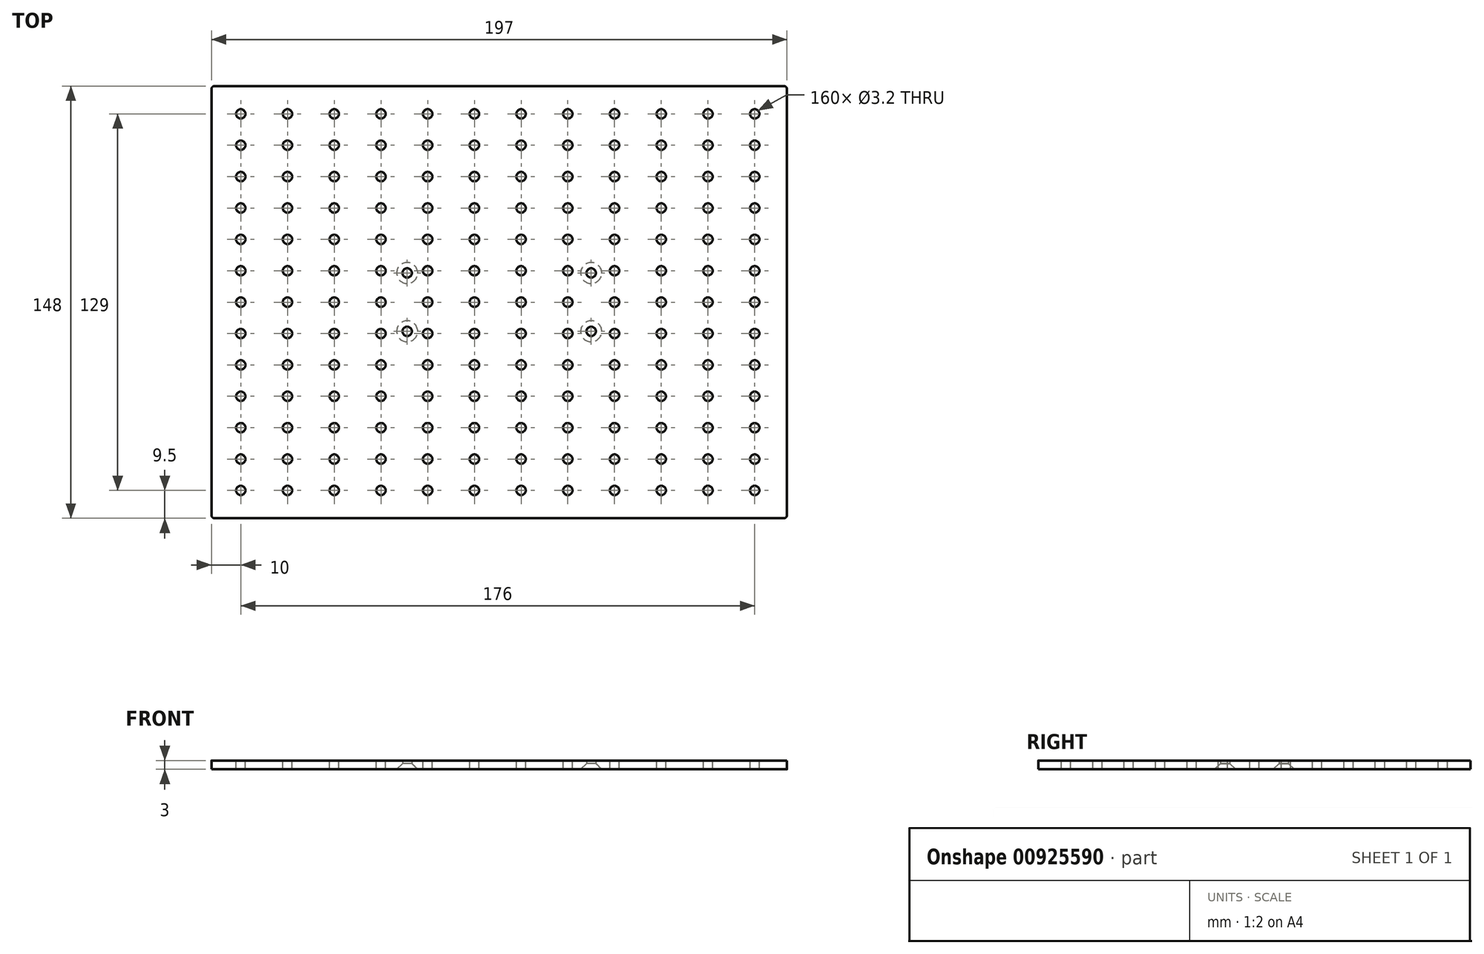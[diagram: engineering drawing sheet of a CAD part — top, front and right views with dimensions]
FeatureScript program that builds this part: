
annotation { "Feature Type Name" : "Feature", "Feature Type Description" : "" }
export const myFeature = defineFeature(function(context is Context, id is Id, definition is map)
    precondition{}
    {
        {
            var Q0;
            Q0=qCreatedBy(makeId("Top.planeOp"),FACE);
            var sketch = newSketch(context, id + "F0", { "sketchPlane" : qUnion([Q0])});
            skLineSegment(sketch, "E0.bottom", {"start": v(98.5, -74) * mm, "end": v(-98.5, -74) * mm});
            skLineSegment(sketch, "E0.top", {"start": v(98.5, 74) * mm, "end": v(-98.5, 74) * mm});
            skLineSegment(sketch, "E0.left", {"start": v(98.5, -74) * mm, "end": v(98.5, 74) * mm});
            skLineSegment(sketch, "E0.right", {"start": v(-98.5, -74) * mm, "end": v(-98.5, 74) * mm});
            skPoint(sketch, "E0.middle", {"position": v(0, 0) * mm});
            skLineSegment(sketch, "E1", {"start": v(0, 19.57) * mm, "end": v(0, -20.96) * mm, "construction": true});
            skLineSegment(sketch, "E2", {"start": v(-19.34, 0) * mm, "end": v(20.32, 0) * mm, "construction": true});
            skCircle(sketch, "E3", {"center": v(-31.5, 10) * mm, "radius": 1.6 * mm});
            skCircle(sketch, "E4", {"center": v(31.5, 10) * mm, "radius": 1.6 * mm});
            skCircle(sketch, "E5", {"center": v(31.5, -10) * mm, "radius": 1.6 * mm});
            skCircle(sketch, "E6", {"center": v(-31.5, -10) * mm, "radius": 1.6 * mm});
            skSolve(sketch);
        }
        {
            var Q0;
            Q0 = qSketchRegion(id + "F0", true);
            extrude(context, id + "F1", {"entities" : qUnion([Q0]), "depth" : 3 * mm, "offsetDistance" : 25 * mm});
        }
        {
            var Q0;
            Q0=makeQuery(id+"F1.opExtrude","CAP_FACE",FACE,{"disambiguationData":[OSD([sQuery(id+"F0.wireOp",EDGE,"E0.bottom"),sQuery(id+"F0.wireOp",EDGE,"E0.top"),sQuery(id+"F0.wireOp",EDGE,"E0.left"),sQuery(id+"F0.wireOp",EDGE,"E0.right"),sQuery(id+"F0.wireOp",EDGE,"E3"),sQuery(id+"F0.wireOp",EDGE,"E4"),sQuery(id+"F0.wireOp",EDGE,"E5"),sQuery(id+"F0.wireOp",EDGE,"E6")])],"isStart":false});
            var sketch = newSketch(context, id + "F2", { "sketchPlane" : qUnion([Q0])});
            skCircle(sketch, "E7", {"center": v(-88.5, 0) * mm, "radius": 1.6 * mm});
            skLineSegment(sketch, "E8.direction1", {"start": v(-88.5, 0) * mm, "end": v(-70.75, 0) * mm, "construction": true});
            skCircle(sketch, "E9.0.1.0", {"center": v(-88.5, 10.75) * mm, "radius": 1.6 * mm});
            skCircle(sketch, "E9.0.2.0", {"center": v(-88.5, 21.5) * mm, "radius": 1.6 * mm});
            skCircle(sketch, "E9.0.3.0", {"center": v(-88.5, 32.25) * mm, "radius": 1.6 * mm});
            skCircle(sketch, "E9.0.4.0", {"center": v(-88.5, 43) * mm, "radius": 1.6 * mm});
            skCircle(sketch, "E9.0.5.0", {"center": v(-88.5, 53.75) * mm, "radius": 1.6 * mm});
            skCircle(sketch, "E9.0.6.0", {"center": v(-88.5, 64.5) * mm, "radius": 1.6 * mm});
            skLineSegment(sketch, "E9.direction1", {"start": v(-88.5, 0) * mm, "end": v(-63.5, 0) * mm, "construction": true});
            skLineSegment(sketch, "E9.direction2", {"start": v(-88.5, 0) * mm, "end": v(-88.5, 10.75) * mm, "construction": true});
            skCircle(sketch, "E10.0.1.0", {"center": v(-88.5, -10.75) * mm, "radius": 1.6 * mm});
            skCircle(sketch, "E10.0.2.0", {"center": v(-88.5, -21.5) * mm, "radius": 1.6 * mm});
            skCircle(sketch, "E10.0.3.0", {"center": v(-88.5, -32.25) * mm, "radius": 1.6 * mm});
            skCircle(sketch, "E10.0.4.0", {"center": v(-88.5, -43) * mm, "radius": 1.6 * mm});
            skCircle(sketch, "E10.0.5.0", {"center": v(-88.5, -53.75) * mm, "radius": 1.6 * mm});
            skCircle(sketch, "E10.0.6.0", {"center": v(-88.5, -64.5) * mm, "radius": 1.6 * mm});
            skLineSegment(sketch, "E10.direction2", {"start": v(-88.5, 0) * mm, "end": v(-88.5, -10.75) * mm, "construction": true});
            skCircle(sketch, "E11.1.0.0", {"center": v(-72.5, 0) * mm, "radius": 1.6 * mm});
            skCircle(sketch, "E11.1.0.1", {"center": v(-72.5, -10.75) * mm, "radius": 1.6 * mm});
            skCircle(sketch, "E11.1.0.2", {"center": v(-72.5, 10.75) * mm, "radius": 1.6 * mm});
            skCircle(sketch, "E11.1.0.3", {"center": v(-72.5, -32.25) * mm, "radius": 1.6 * mm});
            skCircle(sketch, "E11.1.0.4", {"center": v(-72.5, -53.75) * mm, "radius": 1.6 * mm});
            skCircle(sketch, "E11.1.0.5", {"center": v(-72.5, -64.5) * mm, "radius": 1.6 * mm});
            skCircle(sketch, "E11.1.0.6", {"center": v(-72.5, -43) * mm, "radius": 1.6 * mm});
            skCircle(sketch, "E11.1.0.7", {"center": v(-72.5, -21.5) * mm, "radius": 1.6 * mm});
            skCircle(sketch, "E11.1.0.8", {"center": v(-72.5, 64.5) * mm, "radius": 1.6 * mm});
            skCircle(sketch, "E11.1.0.9", {"center": v(-72.5, 43) * mm, "radius": 1.6 * mm});
            skCircle(sketch, "E11.1.0.10", {"center": v(-72.5, 21.5) * mm, "radius": 1.6 * mm});
            skCircle(sketch, "E11.1.0.11", {"center": v(-72.5, 32.25) * mm, "radius": 1.6 * mm});
            skCircle(sketch, "E11.1.0.12", {"center": v(-72.5, 53.75) * mm, "radius": 1.6 * mm});
            skCircle(sketch, "E11.2.0.0", {"center": v(-56.5, 0) * mm, "radius": 1.6 * mm});
            skCircle(sketch, "E11.2.0.1", {"center": v(-56.5, -10.75) * mm, "radius": 1.6 * mm});
            skCircle(sketch, "E11.2.0.2", {"center": v(-56.5, 10.75) * mm, "radius": 1.6 * mm});
            skCircle(sketch, "E11.2.0.3", {"center": v(-56.5, -32.25) * mm, "radius": 1.6 * mm});
            skCircle(sketch, "E11.2.0.4", {"center": v(-56.5, -53.75) * mm, "radius": 1.6 * mm});
            skCircle(sketch, "E11.2.0.5", {"center": v(-56.5, -64.5) * mm, "radius": 1.6 * mm});
            skCircle(sketch, "E11.2.0.6", {"center": v(-56.5, -43) * mm, "radius": 1.6 * mm});
            skCircle(sketch, "E11.2.0.7", {"center": v(-56.5, -21.5) * mm, "radius": 1.6 * mm});
            skCircle(sketch, "E11.2.0.8", {"center": v(-56.5, 64.5) * mm, "radius": 1.6 * mm});
            skCircle(sketch, "E11.2.0.9", {"center": v(-56.5, 43) * mm, "radius": 1.6 * mm});
            skCircle(sketch, "E11.2.0.10", {"center": v(-56.5, 21.5) * mm, "radius": 1.6 * mm});
            skCircle(sketch, "E11.2.0.11", {"center": v(-56.5, 32.25) * mm, "radius": 1.6 * mm});
            skCircle(sketch, "E11.2.0.12", {"center": v(-56.5, 53.75) * mm, "radius": 1.6 * mm});
            skCircle(sketch, "E11.3.0.0", {"center": v(-40.5, 0) * mm, "radius": 1.6 * mm});
            skCircle(sketch, "E11.3.0.1", {"center": v(-40.5, -10.75) * mm, "radius": 1.6 * mm});
            skCircle(sketch, "E11.3.0.2", {"center": v(-40.5, 10.75) * mm, "radius": 1.6 * mm});
            skCircle(sketch, "E11.3.0.3", {"center": v(-40.5, -32.25) * mm, "radius": 1.6 * mm});
            skCircle(sketch, "E11.3.0.4", {"center": v(-40.5, -53.75) * mm, "radius": 1.6 * mm});
            skCircle(sketch, "E11.3.0.5", {"center": v(-40.5, -64.5) * mm, "radius": 1.6 * mm});
            skCircle(sketch, "E11.3.0.6", {"center": v(-40.5, -43) * mm, "radius": 1.6 * mm});
            skCircle(sketch, "E11.3.0.7", {"center": v(-40.5, -21.5) * mm, "radius": 1.6 * mm});
            skCircle(sketch, "E11.3.0.8", {"center": v(-40.5, 64.5) * mm, "radius": 1.6 * mm});
            skCircle(sketch, "E11.3.0.9", {"center": v(-40.5, 43) * mm, "radius": 1.6 * mm});
            skCircle(sketch, "E11.3.0.10", {"center": v(-40.5, 21.5) * mm, "radius": 1.6 * mm});
            skCircle(sketch, "E11.3.0.11", {"center": v(-40.5, 32.25) * mm, "radius": 1.6 * mm});
            skCircle(sketch, "E11.3.0.12", {"center": v(-40.5, 53.75) * mm, "radius": 1.6 * mm});
            skCircle(sketch, "E11.4.0.0", {"center": v(-24.5, 0) * mm, "radius": 1.6 * mm});
            skCircle(sketch, "E11.4.0.1", {"center": v(-24.5, -10.75) * mm, "radius": 1.6 * mm});
            skCircle(sketch, "E11.4.0.2", {"center": v(-24.5, 10.75) * mm, "radius": 1.6 * mm});
            skCircle(sketch, "E11.4.0.3", {"center": v(-24.5, -32.25) * mm, "radius": 1.6 * mm});
            skCircle(sketch, "E11.4.0.4", {"center": v(-24.5, -53.75) * mm, "radius": 1.6 * mm});
            skCircle(sketch, "E11.4.0.5", {"center": v(-24.5, -64.5) * mm, "radius": 1.6 * mm});
            skCircle(sketch, "E11.4.0.6", {"center": v(-24.5, -43) * mm, "radius": 1.6 * mm});
            skCircle(sketch, "E11.4.0.7", {"center": v(-24.5, -21.5) * mm, "radius": 1.6 * mm});
            skCircle(sketch, "E11.4.0.8", {"center": v(-24.5, 64.5) * mm, "radius": 1.6 * mm});
            skCircle(sketch, "E11.4.0.9", {"center": v(-24.5, 43) * mm, "radius": 1.6 * mm});
            skCircle(sketch, "E11.4.0.10", {"center": v(-24.5, 21.5) * mm, "radius": 1.6 * mm});
            skCircle(sketch, "E11.4.0.11", {"center": v(-24.5, 32.25) * mm, "radius": 1.6 * mm});
            skCircle(sketch, "E11.4.0.12", {"center": v(-24.5, 53.75) * mm, "radius": 1.6 * mm});
            skCircle(sketch, "E11.5.0.0", {"center": v(-8.5, 0) * mm, "radius": 1.6 * mm});
            skCircle(sketch, "E11.5.0.1", {"center": v(-8.5, -10.75) * mm, "radius": 1.6 * mm});
            skCircle(sketch, "E11.5.0.2", {"center": v(-8.5, 10.75) * mm, "radius": 1.6 * mm});
            skCircle(sketch, "E11.5.0.3", {"center": v(-8.5, -32.25) * mm, "radius": 1.6 * mm});
            skCircle(sketch, "E11.5.0.4", {"center": v(-8.5, -53.75) * mm, "radius": 1.6 * mm});
            skCircle(sketch, "E11.5.0.5", {"center": v(-8.5, -64.5) * mm, "radius": 1.6 * mm});
            skCircle(sketch, "E11.5.0.6", {"center": v(-8.5, -43) * mm, "radius": 1.6 * mm});
            skCircle(sketch, "E11.5.0.7", {"center": v(-8.5, -21.5) * mm, "radius": 1.6 * mm});
            skCircle(sketch, "E11.5.0.8", {"center": v(-8.5, 64.5) * mm, "radius": 1.6 * mm});
            skCircle(sketch, "E11.5.0.9", {"center": v(-8.5, 43) * mm, "radius": 1.6 * mm});
            skCircle(sketch, "E11.5.0.10", {"center": v(-8.5, 21.5) * mm, "radius": 1.6 * mm});
            skCircle(sketch, "E11.5.0.11", {"center": v(-8.5, 32.25) * mm, "radius": 1.6 * mm});
            skCircle(sketch, "E11.5.0.12", {"center": v(-8.5, 53.75) * mm, "radius": 1.6 * mm});
            skCircle(sketch, "E11.6.0.0", {"center": v(7.5, 0) * mm, "radius": 1.6 * mm});
            skCircle(sketch, "E11.6.0.1", {"center": v(7.5, -10.75) * mm, "radius": 1.6 * mm});
            skCircle(sketch, "E11.6.0.2", {"center": v(7.5, 10.75) * mm, "radius": 1.6 * mm});
            skCircle(sketch, "E11.6.0.3", {"center": v(7.5, -32.25) * mm, "radius": 1.6 * mm});
            skCircle(sketch, "E11.6.0.4", {"center": v(7.5, -53.75) * mm, "radius": 1.6 * mm});
            skCircle(sketch, "E11.6.0.5", {"center": v(7.5, -64.5) * mm, "radius": 1.6 * mm});
            skCircle(sketch, "E11.6.0.6", {"center": v(7.5, -43) * mm, "radius": 1.6 * mm});
            skCircle(sketch, "E11.6.0.7", {"center": v(7.5, -21.5) * mm, "radius": 1.6 * mm});
            skCircle(sketch, "E11.6.0.8", {"center": v(7.5, 64.5) * mm, "radius": 1.6 * mm});
            skCircle(sketch, "E11.6.0.9", {"center": v(7.5, 43) * mm, "radius": 1.6 * mm});
            skCircle(sketch, "E11.6.0.10", {"center": v(7.5, 21.5) * mm, "radius": 1.6 * mm});
            skCircle(sketch, "E11.6.0.11", {"center": v(7.5, 32.25) * mm, "radius": 1.6 * mm});
            skCircle(sketch, "E11.6.0.12", {"center": v(7.5, 53.75) * mm, "radius": 1.6 * mm});
            skCircle(sketch, "E11.7.0.0", {"center": v(23.5, 0) * mm, "radius": 1.6 * mm});
            skCircle(sketch, "E11.7.0.1", {"center": v(23.5, -10.75) * mm, "radius": 1.6 * mm});
            skCircle(sketch, "E11.7.0.2", {"center": v(23.5, 10.75) * mm, "radius": 1.6 * mm});
            skCircle(sketch, "E11.7.0.3", {"center": v(23.5, -32.25) * mm, "radius": 1.6 * mm});
            skCircle(sketch, "E11.7.0.4", {"center": v(23.5, -53.75) * mm, "radius": 1.6 * mm});
            skCircle(sketch, "E11.7.0.5", {"center": v(23.5, -64.5) * mm, "radius": 1.6 * mm});
            skCircle(sketch, "E11.7.0.6", {"center": v(23.5, -43) * mm, "radius": 1.6 * mm});
            skCircle(sketch, "E11.7.0.7", {"center": v(23.5, -21.5) * mm, "radius": 1.6 * mm});
            skCircle(sketch, "E11.7.0.8", {"center": v(23.5, 64.5) * mm, "radius": 1.6 * mm});
            skCircle(sketch, "E11.7.0.9", {"center": v(23.5, 43) * mm, "radius": 1.6 * mm});
            skCircle(sketch, "E11.7.0.10", {"center": v(23.5, 21.5) * mm, "radius": 1.6 * mm});
            skCircle(sketch, "E11.7.0.11", {"center": v(23.5, 32.25) * mm, "radius": 1.6 * mm});
            skCircle(sketch, "E11.7.0.12", {"center": v(23.5, 53.75) * mm, "radius": 1.6 * mm});
            skCircle(sketch, "E11.8.0.0", {"center": v(39.5, 0) * mm, "radius": 1.6 * mm});
            skCircle(sketch, "E11.8.0.1", {"center": v(39.5, -10.75) * mm, "radius": 1.6 * mm});
            skCircle(sketch, "E11.8.0.2", {"center": v(39.5, 10.75) * mm, "radius": 1.6 * mm});
            skCircle(sketch, "E11.8.0.3", {"center": v(39.5, -32.25) * mm, "radius": 1.6 * mm});
            skCircle(sketch, "E11.8.0.4", {"center": v(39.5, -53.75) * mm, "radius": 1.6 * mm});
            skCircle(sketch, "E11.8.0.5", {"center": v(39.5, -64.5) * mm, "radius": 1.6 * mm});
            skCircle(sketch, "E11.8.0.6", {"center": v(39.5, -43) * mm, "radius": 1.6 * mm});
            skCircle(sketch, "E11.8.0.7", {"center": v(39.5, -21.5) * mm, "radius": 1.6 * mm});
            skCircle(sketch, "E11.8.0.8", {"center": v(39.5, 64.5) * mm, "radius": 1.6 * mm});
            skCircle(sketch, "E11.8.0.9", {"center": v(39.5, 43) * mm, "radius": 1.6 * mm});
            skCircle(sketch, "E11.8.0.10", {"center": v(39.5, 21.5) * mm, "radius": 1.6 * mm});
            skCircle(sketch, "E11.8.0.11", {"center": v(39.5, 32.25) * mm, "radius": 1.6 * mm});
            skCircle(sketch, "E11.8.0.12", {"center": v(39.5, 53.75) * mm, "radius": 1.6 * mm});
            skCircle(sketch, "E11.9.0.0", {"center": v(55.5, 0) * mm, "radius": 1.6 * mm});
            skCircle(sketch, "E11.9.0.1", {"center": v(55.5, -10.75) * mm, "radius": 1.6 * mm});
            skCircle(sketch, "E11.9.0.2", {"center": v(55.5, 10.75) * mm, "radius": 1.6 * mm});
            skCircle(sketch, "E11.9.0.3", {"center": v(55.5, -32.25) * mm, "radius": 1.6 * mm});
            skCircle(sketch, "E11.9.0.4", {"center": v(55.5, -53.75) * mm, "radius": 1.6 * mm});
            skCircle(sketch, "E11.9.0.5", {"center": v(55.5, -64.5) * mm, "radius": 1.6 * mm});
            skCircle(sketch, "E11.9.0.6", {"center": v(55.5, -43) * mm, "radius": 1.6 * mm});
            skCircle(sketch, "E11.9.0.7", {"center": v(55.5, -21.5) * mm, "radius": 1.6 * mm});
            skCircle(sketch, "E11.9.0.8", {"center": v(55.5, 64.5) * mm, "radius": 1.6 * mm});
            skCircle(sketch, "E11.9.0.9", {"center": v(55.5, 43) * mm, "radius": 1.6 * mm});
            skCircle(sketch, "E11.9.0.10", {"center": v(55.5, 21.5) * mm, "radius": 1.6 * mm});
            skCircle(sketch, "E11.9.0.11", {"center": v(55.5, 32.25) * mm, "radius": 1.6 * mm});
            skCircle(sketch, "E11.9.0.12", {"center": v(55.5, 53.75) * mm, "radius": 1.6 * mm});
            skCircle(sketch, "E11.10.0.0", {"center": v(71.5, 0) * mm, "radius": 1.6 * mm});
            skCircle(sketch, "E11.10.0.1", {"center": v(71.5, -10.75) * mm, "radius": 1.6 * mm});
            skCircle(sketch, "E11.10.0.2", {"center": v(71.5, 10.75) * mm, "radius": 1.6 * mm});
            skCircle(sketch, "E11.10.0.3", {"center": v(71.5, -32.25) * mm, "radius": 1.6 * mm});
            skCircle(sketch, "E11.10.0.4", {"center": v(71.5, -53.75) * mm, "radius": 1.6 * mm});
            skCircle(sketch, "E11.10.0.5", {"center": v(71.5, -64.5) * mm, "radius": 1.6 * mm});
            skCircle(sketch, "E11.10.0.6", {"center": v(71.5, -43) * mm, "radius": 1.6 * mm});
            skCircle(sketch, "E11.10.0.7", {"center": v(71.5, -21.5) * mm, "radius": 1.6 * mm});
            skCircle(sketch, "E11.10.0.8", {"center": v(71.5, 64.5) * mm, "radius": 1.6 * mm});
            skCircle(sketch, "E11.10.0.9", {"center": v(71.5, 43) * mm, "radius": 1.6 * mm});
            skCircle(sketch, "E11.10.0.10", {"center": v(71.5, 21.5) * mm, "radius": 1.6 * mm});
            skCircle(sketch, "E11.10.0.11", {"center": v(71.5, 32.25) * mm, "radius": 1.6 * mm});
            skCircle(sketch, "E11.10.0.12", {"center": v(71.5, 53.75) * mm, "radius": 1.6 * mm});
            skCircle(sketch, "E11.11.0.0", {"center": v(87.5, 0) * mm, "radius": 1.6 * mm});
            skCircle(sketch, "E11.11.0.1", {"center": v(87.5, -10.75) * mm, "radius": 1.6 * mm});
            skCircle(sketch, "E11.11.0.2", {"center": v(87.5, 10.75) * mm, "radius": 1.6 * mm});
            skCircle(sketch, "E11.11.0.3", {"center": v(87.5, -32.25) * mm, "radius": 1.6 * mm});
            skCircle(sketch, "E11.11.0.4", {"center": v(87.5, -53.75) * mm, "radius": 1.6 * mm});
            skCircle(sketch, "E11.11.0.5", {"center": v(87.5, -64.5) * mm, "radius": 1.6 * mm});
            skCircle(sketch, "E11.11.0.6", {"center": v(87.5, -43) * mm, "radius": 1.6 * mm});
            skCircle(sketch, "E11.11.0.7", {"center": v(87.5, -21.5) * mm, "radius": 1.6 * mm});
            skCircle(sketch, "E11.11.0.8", {"center": v(87.5, 64.5) * mm, "radius": 1.6 * mm});
            skCircle(sketch, "E11.11.0.9", {"center": v(87.5, 43) * mm, "radius": 1.6 * mm});
            skCircle(sketch, "E11.11.0.10", {"center": v(87.5, 21.5) * mm, "radius": 1.6 * mm});
            skCircle(sketch, "E11.11.0.11", {"center": v(87.5, 32.25) * mm, "radius": 1.6 * mm});
            skCircle(sketch, "E11.11.0.12", {"center": v(87.5, 53.75) * mm, "radius": 1.6 * mm});
            skLineSegment(sketch, "E11.direction1", {"start": v(-88.5, -64.5) * mm, "end": v(-72.5, -64.5) * mm, "construction": true});
            skSolve(sketch);
        }
        {
            var Q0;
            Q0 = qSketchRegion(id + "F2", true);
            extrude(context, id + "F3", {"entities" : qUnion([Q0]), "operationType" : NewBodyOperationType.REMOVE, "oppositeDirection" : true, "depth" : 25 * mm, "offsetDistance" : 25 * mm});
        }
        {
            var Q0;
            Q0=makeQuery(id+"F1.opExtrude","SWEPT_EDGE",EDGE,{"disambiguationData":[OSD([sQuery(id+"F0.wireOp",EDGE,"E0.bottom"),sQuery(id+"F0.wireOp",EDGE,"E0.right")])]});
            var Q1;
            Q1=makeQuery(id+"F1.opExtrude","SWEPT_EDGE",EDGE,{"disambiguationData":[OSD([sQuery(id+"F0.wireOp",EDGE,"E0.bottom"),sQuery(id+"F0.wireOp",EDGE,"E0.left")])]});
            var Q2;
            Q2=makeQuery(id+"F1.opExtrude","SWEPT_EDGE",EDGE,{"disambiguationData":[OSD([sQuery(id+"F0.wireOp",EDGE,"E0.top"),sQuery(id+"F0.wireOp",EDGE,"E0.right")])]});
            var Q3;
            Q3=makeQuery(id+"F1.opExtrude","SWEPT_EDGE",EDGE,{"disambiguationData":[OSD([sQuery(id+"F0.wireOp",EDGE,"E0.top"),sQuery(id+"F0.wireOp",EDGE,"E0.left")])]});
            fillet(context, id + "F4", {"entities" : qUnion([Q0, Q1, Q2, Q3]), "radius" : 1 * mm, "tangentPropagation" : true, "allowEdgeOverflow" : false});
        }
        {
            var Q0;
            Q0=makeQuery(id+"F1.opExtrude","CAP_EDGE",EDGE,{"disambiguationData":[OSD([sQuery(id+"F0.wireOp",EDGE,"E6")])],"isStart":true});
            var Q1;
            Q1=makeQuery(id+"F1.opExtrude","CAP_EDGE",EDGE,{"disambiguationData":[OSD([sQuery(id+"F0.wireOp",EDGE,"E3")])],"isStart":true});
            var Q2;
            Q2=makeQuery(id+"F1.opExtrude","CAP_EDGE",EDGE,{"disambiguationData":[OSD([sQuery(id+"F0.wireOp",EDGE,"E5")])],"isStart":true});
            var Q3;
            Q3=makeQuery(id+"F1.opExtrude","CAP_EDGE",EDGE,{"disambiguationData":[OSD([sQuery(id+"F0.wireOp",EDGE,"E4")])],"isStart":true});
            chamfer(context, id + "F5", {"entities" : qUnion([Q0, Q1, Q2, Q3]), "width" : 2 * mm, "tangentPropagation" : true});
        }
    });
